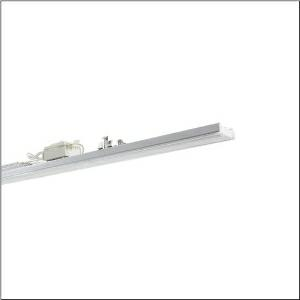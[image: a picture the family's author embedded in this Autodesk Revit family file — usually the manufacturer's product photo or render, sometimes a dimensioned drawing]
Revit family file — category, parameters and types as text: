
# Revit family: licross_11_recessed_mo_51tl12dn4axg3c
name_source: partatom
category: Lighting Fixtures
units: mm (PartAtom-declared; Revit-internal decimal feet)

## family parameters
Cut with Voids When Loaded = No
Host = Face
Light Source = No
Part Type = Normal
Room Calculation Point = No
Round Connector Dimension = Use Diameter
Shared = No

## types (1)
- --- (1 x LED, 1010 lm, 6.7 W, 4000K)
    Apparent Load = 7 VA
    CIE Flux Codes = 67 92 99 100 100
    Color Rendering = 80
    Color Temperature = 4000K
    Default Elevation = 1800 mm
    Description = Licross 11 Recessed MO, luminaire insert, of sheet steel, coil coated, white, length: 1.500mm, width: 66mm, height: 67mm, LED rated luminous flux: 10.240lm, light colour: 840, SDCM (Standard Deviation of Colour Matching)MacAdam ≤ 2 SDCM (initial), control gear: DALI 2 (for two DALI lines), with plug, 6-pole, with phase selection, for trunking rail, 14-core, mains connection: 220..240V, AC, 50/60Hz, rated input power: 61W, for trunking rail, 14-core, internal wiring halogen-free, for emergency light function, converter,control gear: single battery element, battery: LiFePO4, 9Ah, primary optical cover: cover, of PMMA, light emission: direct distribution, primary light characteristic: symmetric, protection rating (complete): IP40, insulation class (complete): insulation class I (protective earthing), certification: CE, UKCA, protection symbol: D if used in an environment without relevant dust loads with corresponding accessories, impact resistance: IK06, permissible ambient temperature for indoor applications: +5..+35°C, standard: EN 60598-2-22, LABS conformity tested according to VDMA 24364:2018-05, reducing of maximum allowable ambient temperature of 5°C with ceiling mounting, corresponds to IFS (International Featured Standards) requirements for safety and quality in the food industry, The light source and the operating device comply with the requirements of the Ecodesign Regulation (EU) 2019/2020 and are replaceable in accordance with this regulation, packaging unit: 1 piece
    Height = 58 mm
    Lamp = 1 x LED
    Lamp Light Flux = 1010 lm
    Lamp Power = 6.7 W
    Lamp count = 1
    Length = 1500 mm
    Luminous efficacy = 151 lm/W
    Manufacturer = Siteco
    ModVariant = No
    Model = 51TL12DN4AXG3C
    Mounting Place = Ceiling
    Mounting Type = Pendant
    Number of Poles = 1
    OnlyDefault = Yes
    Power Factor = 1
    Product Name = Licross 11 Recessed MO
    Product group = luminaire insert | ceiling pendant
    ProductGroupID = 901
    Protection Class = Protection class I
    Protection Degree = IP 40
    RLX_Detail_Level = 1
    RLX_Emergency_Light_Flux = 0 lm
    RLX_Emergency_Type = 0
    RLX_Emergency_Type_DB = No
    RlxData = <blob elided: 25005 chars, md5=5c1af5b7>
    Socket = socket
    Standby Power = 0 W
    System Light Flux = 1010 lm
    System Power = 7 W
    Type Comments = : emergency light operation: 3 h
    Type Image = l_1296930.jpg
    URL = http://relux.com
    VarID = @adj_094105
    Voltage = 0 V
    Weight = 0.00 kg
    Width = 66 mm

## geometry (parser evidence)
native form markers: Blend x4, Sweep x12
no freeform markers — native parametric forms only
